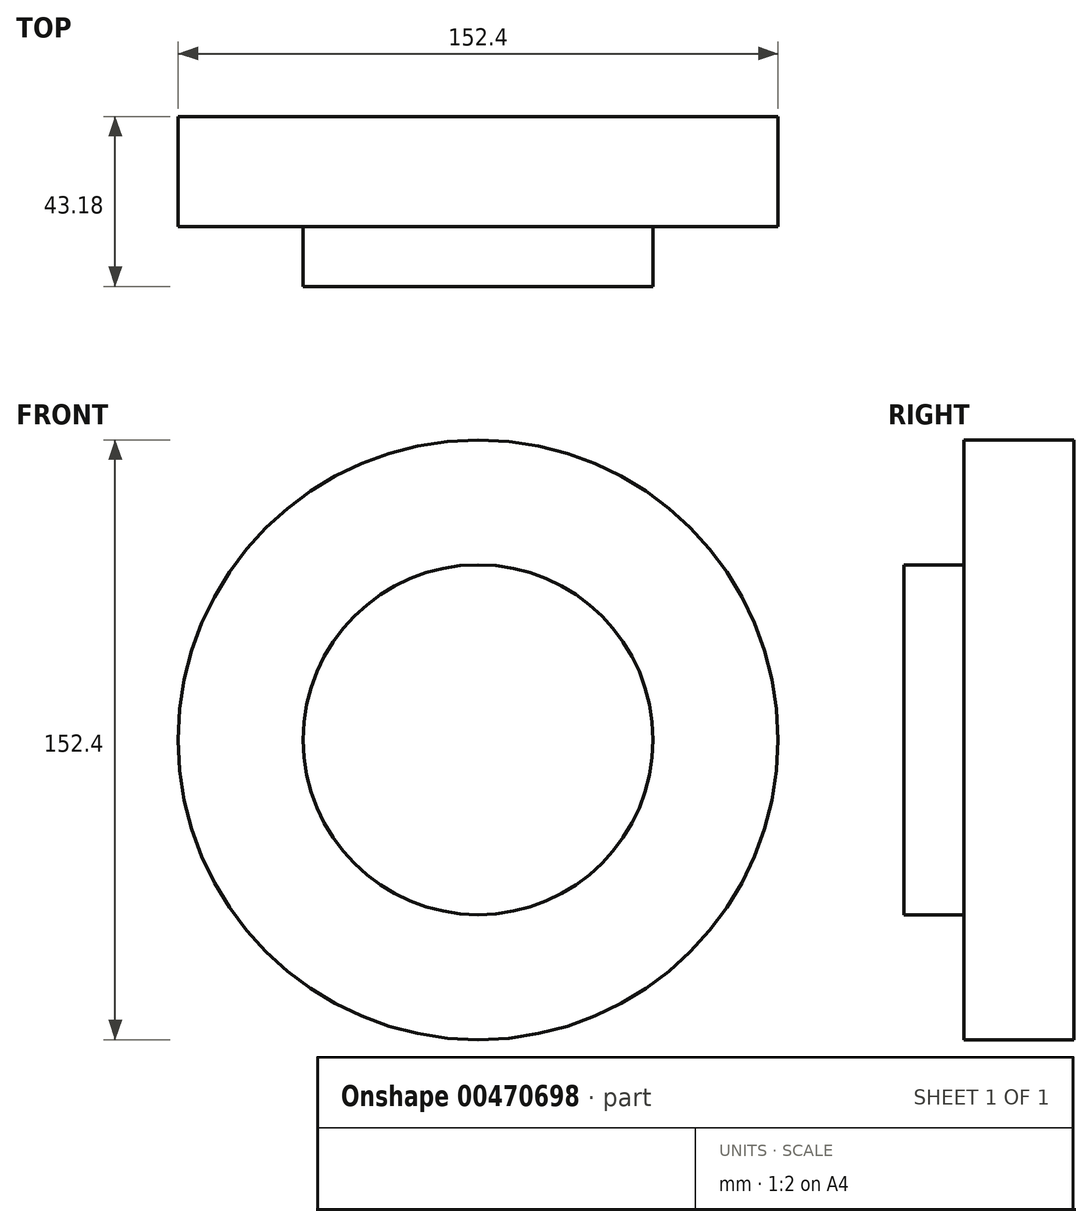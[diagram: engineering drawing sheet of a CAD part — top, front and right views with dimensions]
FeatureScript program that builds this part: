
annotation { "Feature Type Name" : "Feature", "Feature Type Description" : "" }
export const myFeature = defineFeature(function(context is Context, id is Id, definition is map)
    precondition{}
    {
        {
            var Q0;
            Q0=qCreatedBy(makeId("Front.planeOp"),FACE);
            var sketch = newSketch(context, id + "F0", { "sketchPlane" : qUnion([Q0])});
            skCircle(sketch, "E0", {"center": v(0, 0) * mm, "radius": 76.2 * mm});
            skCircle(sketch, "E1", {"center": v(0, 0) * mm, "radius": 44.45 * mm});
            skSolve(sketch);
        }
        {
            var Q0;
            Q0 = qSketchRegion(id + "F0", true);
            extrude(context, id + "F1", {"entities" : qUnion([Q0]), "depth" : 2.54 * mm});
        }
        {
            var Q0;
            Q0=makeQuery(id+"F0.imprint","IMPRINT",FACE,{"disambiguationData":[TD([[makeQuery(id+"F0.imprint","IMPRINT",EDGE,{"derivedFrom":sQuery(id+"F0.wireOp",EDGE,"E1")}),1.0]])]});
            extrude(context, id + "F2", {"entities" : qUnion([Q0]), "operationType" : NewBodyOperationType.ADD, "depth" : 17.78 * mm});
        }
        {
            var Q0;
            Q0=makeQuery(id+"F0.imprint","IMPRINT",FACE,{"disambiguationData":[TD([[makeQuery(id+"F0.imprint","IMPRINT",EDGE,{"derivedFrom":sQuery(id+"F0.wireOp",EDGE,"E1")}),-1.0]])]});
            var Q1;
            Q1=makeQuery(id+"F0.imprint","IMPRINT",FACE,{"disambiguationData":[TD([[makeQuery(id+"F0.imprint","IMPRINT",EDGE,{"derivedFrom":sQuery(id+"F0.wireOp",EDGE,"E1")}),1.0]])]});
            extrude(context, id + "F3", {"entities" : qUnion([Q0, Q1]), "operationType" : NewBodyOperationType.ADD, "oppositeDirection" : true, "depth" : 25.4 * mm});
        }
    });
